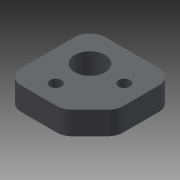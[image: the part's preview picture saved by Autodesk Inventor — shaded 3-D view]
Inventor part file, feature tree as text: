
AUTODESK INVENTOR PART (.ipt)
format: ipt  version: 2013 (Build 170138000, 138)  size: 99,328 bytes
history: native  units: mm
features: extrude x1, sketch x1
ambient origin geometry x8: Origin, YZ Plane, XZ Plane, XY Plane, X Axis, Y Axis, Z Axis, Center Point
bodies: Solid1 (feature_tree)
feature tree (2):
  extrude  "Extrusion1"  [1 undecoded]
  sketch  "Sketch1"  dims[d0=6.0mm d1=0.0mm]
note: 1 required parameter value undecoded (feature->parameter linkage not recoverable at this tier; creation-order binding heuristic only, values carry confidence <= 0.55)
